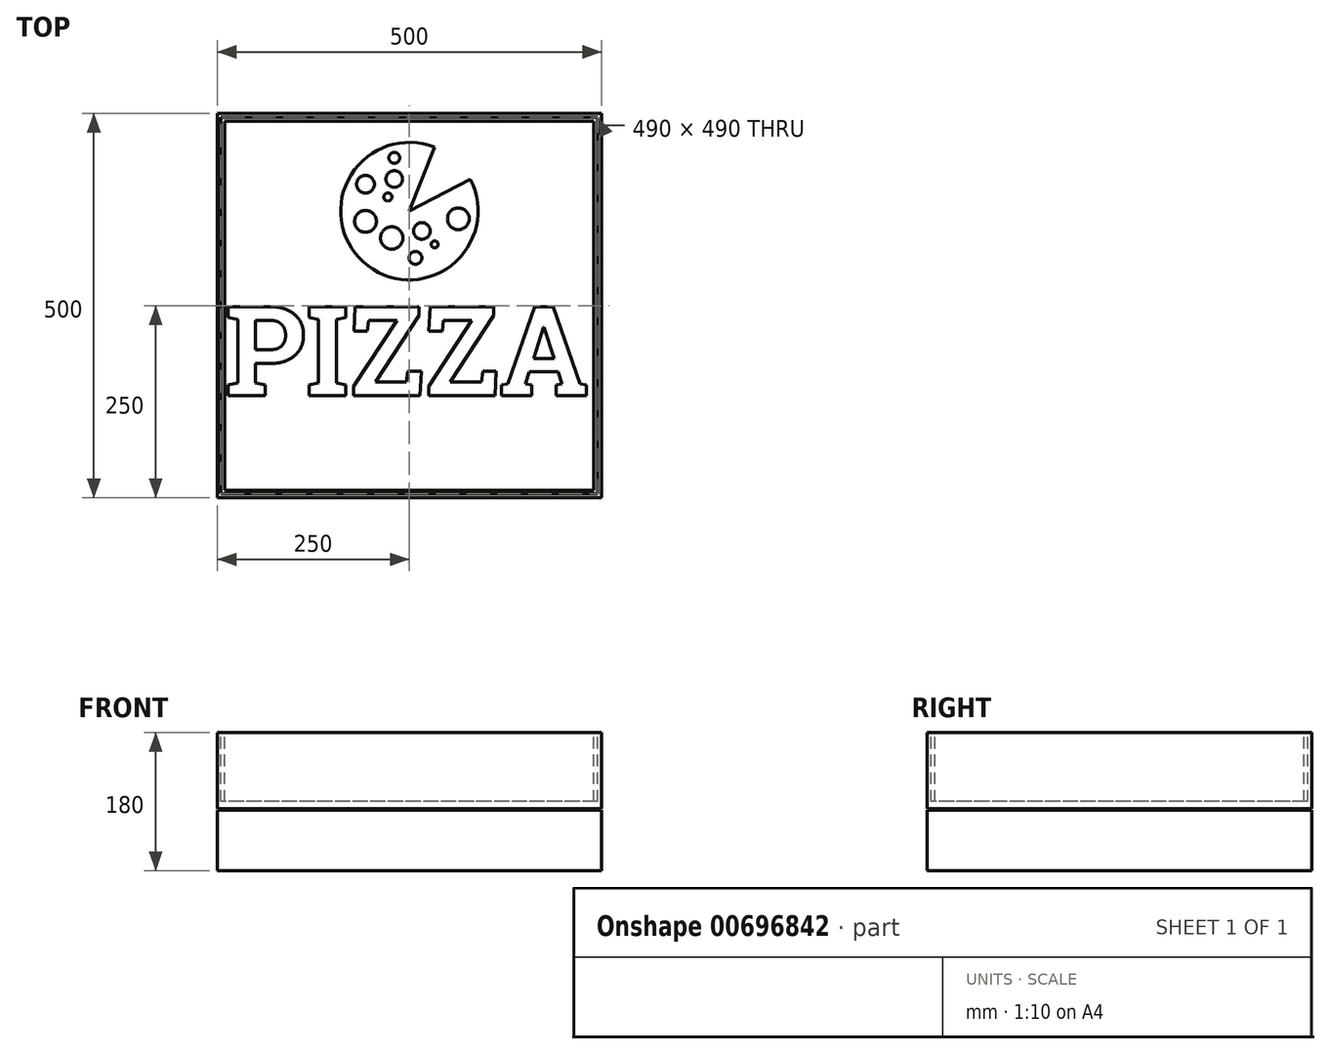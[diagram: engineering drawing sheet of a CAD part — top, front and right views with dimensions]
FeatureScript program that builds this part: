
annotation { "Feature Type Name" : "Feature", "Feature Type Description" : "" }
export const myFeature = defineFeature(function(context is Context, id is Id, definition is map)
    precondition{}
    {
        {
            var Q0;
            Q0=qCreatedBy(makeId("Top.planeOp"),FACE);
            var sketch = newSketch(context, id + "F0", { "sketchPlane" : qUnion([Q0])});
            skLineSegment(sketch, "E0.bottom", {"start": v(250, 250) * mm, "end": v(-250, 250) * mm});
            skLineSegment(sketch, "E0.top", {"start": v(250, -250) * mm, "end": v(-250, -250) * mm});
            skLineSegment(sketch, "E0.left", {"start": v(250, 250) * mm, "end": v(250, -250) * mm});
            skLineSegment(sketch, "E0.right", {"start": v(-250, 250) * mm, "end": v(-250, -250) * mm});
            skPoint(sketch, "E0.middle", {"position": v(0, 0) * mm});
            skSolve(sketch);
        }
        {
            var Q0;
            Q0=makeQuery(id+"F0.imprint","IMPRINT",FACE,{"disambiguationData":[TD([[makeQuery(id+"F0.imprint","IMPRINT",EDGE,{"derivedFrom":sQuery(id+"F0.wireOp",EDGE,"E0.bottom")}),1.0]])]});
            extrude(context, id + "F1", {"entities" : qUnion([Q0]), "depth" : 99 * mm, "offsetDistance" : 25 * mm});
        }
        {
            var Q0;
            Q0=makeQuery(id+"F1.opExtrude","CAP_FACE",FACE,{"disambiguationData":[OSD([sQuery(id+"F0.wireOp",EDGE,"E0.bottom"),sQuery(id+"F0.wireOp",EDGE,"E0.top"),sQuery(id+"F0.wireOp",EDGE,"E0.left"),sQuery(id+"F0.wireOp",EDGE,"E0.right")])],"isStart":false});
            var sketch = newSketch(context, id + "F2", { "sketchPlane" : qUnion([Q0])});
            skLineSegment(sketch, "E1.bottom", {"start": v(245, 245) * mm, "end": v(-245, 245) * mm});
            skLineSegment(sketch, "E1.top", {"start": v(245, -245) * mm, "end": v(-245, -245) * mm});
            skLineSegment(sketch, "E1.left", {"start": v(245, 245) * mm, "end": v(245, -245) * mm});
            skLineSegment(sketch, "E1.right", {"start": v(-245, 245) * mm, "end": v(-245, -245) * mm});
            skPoint(sketch, "E1.middle", {"position": v(0, 0) * mm});
            skSolve(sketch);
        }
        {
            var Q0;
            Q0=makeQuery(id+"F2.imprint","IMPRINT",FACE,{"disambiguationData":[TD([[makeQuery(id+"F2.imprint","IMPRINT",EDGE,{"derivedFrom":sQuery(id+"F2.wireOp",EDGE,"E1.bottom")}),1.0]])]});
            extrude(context, id + "F3", {"entities" : qUnion([Q0]), "operationType" : NewBodyOperationType.ADD, "depth" : 2 * mm, "offsetDistance" : 25 * mm});
        }
        {
            var Q0;
            Q0=makeQuery(id+"F3.opExtrude","CAP_FACE",FACE,{"disambiguationData":[OSD([sQuery(id+"F2.wireOp",EDGE,"E1.bottom"),sQuery(id+"F2.wireOp",EDGE,"E1.top"),sQuery(id+"F2.wireOp",EDGE,"E1.left"),sQuery(id+"F2.wireOp",EDGE,"E1.right")])],"isStart":false});
            var sketch = newSketch(context, id + "F4", { "sketchPlane" : qUnion([Q0])});
            skLineSegment(sketch, "E2.bottom", {"start": v(250, 250) * mm, "end": v(-250, 250) * mm});
            skLineSegment(sketch, "E2.top", {"start": v(250, -250) * mm, "end": v(-250, -250) * mm});
            skLineSegment(sketch, "E2.left", {"start": v(250, 250) * mm, "end": v(250, -250) * mm});
            skLineSegment(sketch, "E2.right", {"start": v(-250, 250) * mm, "end": v(-250, -250) * mm});
            skPoint(sketch, "E2.middle", {"position": v(0, 0) * mm});
            skSolve(sketch);
        }
        {
            var Q0;
            Q0 = qSketchRegion(id + "F4", true);
            extrude(context, id + "F5", {"entities" : qUnion([Q0]), "operationType" : NewBodyOperationType.ADD, "depth" : 99 * mm, "offsetDistance" : 25 * mm});
        }
        {
            var Q0;
            Q0=makeQuery(id+"F5.opExtrude","CAP_FACE",FACE,{"disambiguationData":[OSD([sQuery(id+"F4.wireOp",EDGE,"E2.bottom"),sQuery(id+"F4.wireOp",EDGE,"E2.top"),sQuery(id+"F4.wireOp",EDGE,"E2.left"),sQuery(id+"F4.wireOp",EDGE,"E2.right")])],"isStart":false});
            var sketch = newSketch(context, id + "F6", { "sketchPlane" : qUnion([Q0])});
            skLineSegment(sketch, "E3.bottom", {"start": v(245, 245) * mm, "end": v(-245, 245) * mm});
            skLineSegment(sketch, "E3.top", {"start": v(245, -245) * mm, "end": v(-245, -245) * mm});
            skLineSegment(sketch, "E3.left", {"start": v(245, 245) * mm, "end": v(245, -245) * mm});
            skLineSegment(sketch, "E3.right", {"start": v(-245, 245) * mm, "end": v(-245, -245) * mm});
            skPoint(sketch, "E3.middle", {"position": v(0, 0) * mm});
            skLineSegment(sketch, "E4.bottom", {"start": v(240, 240) * mm, "end": v(-240, 240) * mm});
            skLineSegment(sketch, "E4.top", {"start": v(240, -240) * mm, "end": v(-240, -240) * mm});
            skLineSegment(sketch, "E4.left", {"start": v(240, 240) * mm, "end": v(240, -240) * mm});
            skLineSegment(sketch, "E4.right", {"start": v(-240, 240) * mm, "end": v(-240, -240) * mm});
            skSolve(sketch);
        }
        {
            var Q0;
            Q0=makeQuery(id+"F6.imprint","IMPRINT",FACE,{"disambiguationData":[TD([[makeQuery(id+"F6.imprint","IMPRINT",EDGE,{"derivedFrom":sQuery(id+"F6.wireOp",EDGE,"E3.bottom")}),1.0]])]});
            extrude(context, id + "F7", {"entities" : qUnion([Q0]), "operationType" : NewBodyOperationType.REMOVE, "oppositeDirection" : true, "depth" : 90 * mm, "offsetDistance" : 25 * mm});
        }
        {
            var Q0;
            Q0=makeQuery(id+"F7.boolean.opBoolean","SPLIT",FACE,{"disambiguationData":[TD([makeQuery(id+"F7.opExtrude","SWEPT_FACE",FACE,{"disambiguationData":[OSD([sQuery(id+"F6.wireOp",EDGE,"E4.bottom")])]})])],"derivedFrom":makeQuery(id+"F5.opExtrude","CAP_FACE",FACE,{"disambiguationData":[OSD([sQuery(id+"F4.wireOp",EDGE,"E2.bottom"),sQuery(id+"F4.wireOp",EDGE,"E2.top"),sQuery(id+"F4.wireOp",EDGE,"E2.left"),sQuery(id+"F4.wireOp",EDGE,"E2.right")])],"isStart":false})});
            var sketch = newSketch(context, id + "F8", { "sketchPlane" : qUnion([Q0])});
            skText(sketch, "E5", { "text": "PIZZA", "fontName": "RobotoSlab-Bold.ttf"});
            skCircle(sketch, "E6", {"center": v(0, 122.92) * mm, "radius": 89.35 * mm});
            skLineSegment(sketch, "E7", {"start": v(0, 122.92) * mm, "end": v(33.12, 205.9) * mm});
            skLineSegment(sketch, "E8", {"start": v(0, 122.92) * mm, "end": v(79.32, 164.05) * mm});
            skCircle(sketch, "E9", {"center": v(0, 122.92) * mm, "radius": 98.72 * mm});
            skCircle(sketch, "E10", {"center": v(-27.92, 141.25) * mm, "radius": 5.27 * mm});
            skCircle(sketch, "E11", {"center": v(-19.58, 164.58) * mm, "radius": 10.83 * mm});
            skCircle(sketch, "E12", {"center": v(-57.08, 109.58) * mm, "radius": 14.2 * mm});
            skCircle(sketch, "E13", {"center": v(-22.92, 87.92) * mm, "radius": 14.55 * mm});
            skCircle(sketch, "E14", {"center": v(32.92, 79.58) * mm, "radius": 4.49 * mm});
            skCircle(sketch, "E15", {"center": v(16.25, 97.08) * mm, "radius": 10.87 * mm});
            skCircle(sketch, "E16", {"center": v(63.75, 112.92) * mm, "radius": 14.17 * mm});
            skCircle(sketch, "E17", {"center": v(7.92, 62.08) * mm, "radius": 8.37 * mm});
            skCircle(sketch, "E18", {"center": v(-57.08, 157.92) * mm, "radius": 11.58 * mm});
            skCircle(sketch, "E19", {"center": v(-19.58, 192.08) * mm, "radius": 7.12 * mm});
            const initialGuessF8  = {"E5": [-0.24, -0.11706, 1, 0, 0.11706]};
            skSetInitialGuess(sketch, initialGuessF8);
            skSolve(sketch);
        }
        {
            var Q0;
            Q0=makeQuery(id+"F8.imprint","IMPRINT",FACE,{"disambiguationData":[TD([[makeQuery(id+"F8.imprint","IMPRINT",EDGE,{"derivedFrom":sQuery(id+"F8.wireOp",EDGE,"E5.sketch_text.stroke-0")}),-1.0]])]});
            var Q1;
            Q1=makeQuery(id+"F8.imprint","IMPRINT",FACE,{"disambiguationData":[TD([[makeQuery(id+"F8.imprint","IMPRINT",EDGE,{"derivedFrom":sQuery(id+"F8.wireOp",EDGE,"E5.sketch_text.stroke-23")}),-1.0]])]});
            var Q2;
            Q2=makeQuery(id+"F8.imprint","IMPRINT",FACE,{"disambiguationData":[TD([[makeQuery(id+"F8.imprint","IMPRINT",EDGE,{"derivedFrom":sQuery(id+"F8.wireOp",EDGE,"E5.sketch_text.stroke-35")}),-1.0]])]});
            var Q3;
            Q3=makeQuery(id+"F8.imprint","IMPRINT",FACE,{"disambiguationData":[TD([[makeQuery(id+"F8.imprint","IMPRINT",EDGE,{"derivedFrom":sQuery(id+"F8.wireOp",EDGE,"E5.sketch_text.stroke-49")}),-1.0]])]});
            var Q4;
            Q4=makeQuery(id+"F8.imprint","IMPRINT",FACE,{"disambiguationData":[TD([[makeQuery(id+"F8.imprint","IMPRINT",EDGE,{"derivedFrom":sQuery(id+"F8.wireOp",EDGE,"E5.sketch_text.stroke-63")}),-1.0]])]});
            var Q5;
            {var subQ0=sQuery(id+"F8.wireOp",EDGE,"E7");Q5=makeQuery(id+"F8.imprint","IMPRINT",FACE,{"disambiguationData":[TD([[makeQuery(id+"F8.imprint","IMPRINT",EDGE,{"derivedFrom":subQ0}),1.0]])]});}
            extrude(context, id + "F9", {"entities" : qUnion([Q0, Q1, Q2, Q3, Q4, Q5]), "operationType" : NewBodyOperationType.REMOVE, "oppositeDirection" : true, "depth" : 1 * mm, "offsetDistance" : 25 * mm});
        }
        {
            var Q0;
            Q0=makeQuery(id+"F1.opExtrude","SWEPT_FACE",FACE,{"disambiguationData":[OSD([sQuery(id+"F0.wireOp",EDGE,"E0.right")])]});
            var sketch = newSketch(context, id + "F10", { "sketchPlane" : qUnion([Q0])});
            skLineSegment(sketch, "E20.bottom", {"start": v(-250, 0) * mm, "end": v(250, 0) * mm});
            skLineSegment(sketch, "E20.top", {"start": v(-250, 20) * mm, "end": v(250, 20) * mm});
            skLineSegment(sketch, "E20.left", {"start": v(-250, 0) * mm, "end": v(-250, 20) * mm});
            skLineSegment(sketch, "E20.right", {"start": v(250, 0) * mm, "end": v(250, 20) * mm});
            skSolve(sketch);
        }
        {
            var Q0;
            Q0=makeQuery(id+"F10.imprint","IMPRINT",FACE,{"disambiguationData":[TD([[makeQuery(id+"F10.imprint","IMPRINT",EDGE,{"derivedFrom":sQuery(id+"F10.wireOp",EDGE,"E20.bottom")}),1.0]])]});
            extrude(context, id + "F11", {"entities" : qUnion([Q0]), "operationType" : NewBodyOperationType.REMOVE, "endBound" : BoundingType.THROUGH_ALL, "oppositeDirection" : true, "depth" : 25 * mm, "offsetDistance" : 25 * mm});
        }
    });
